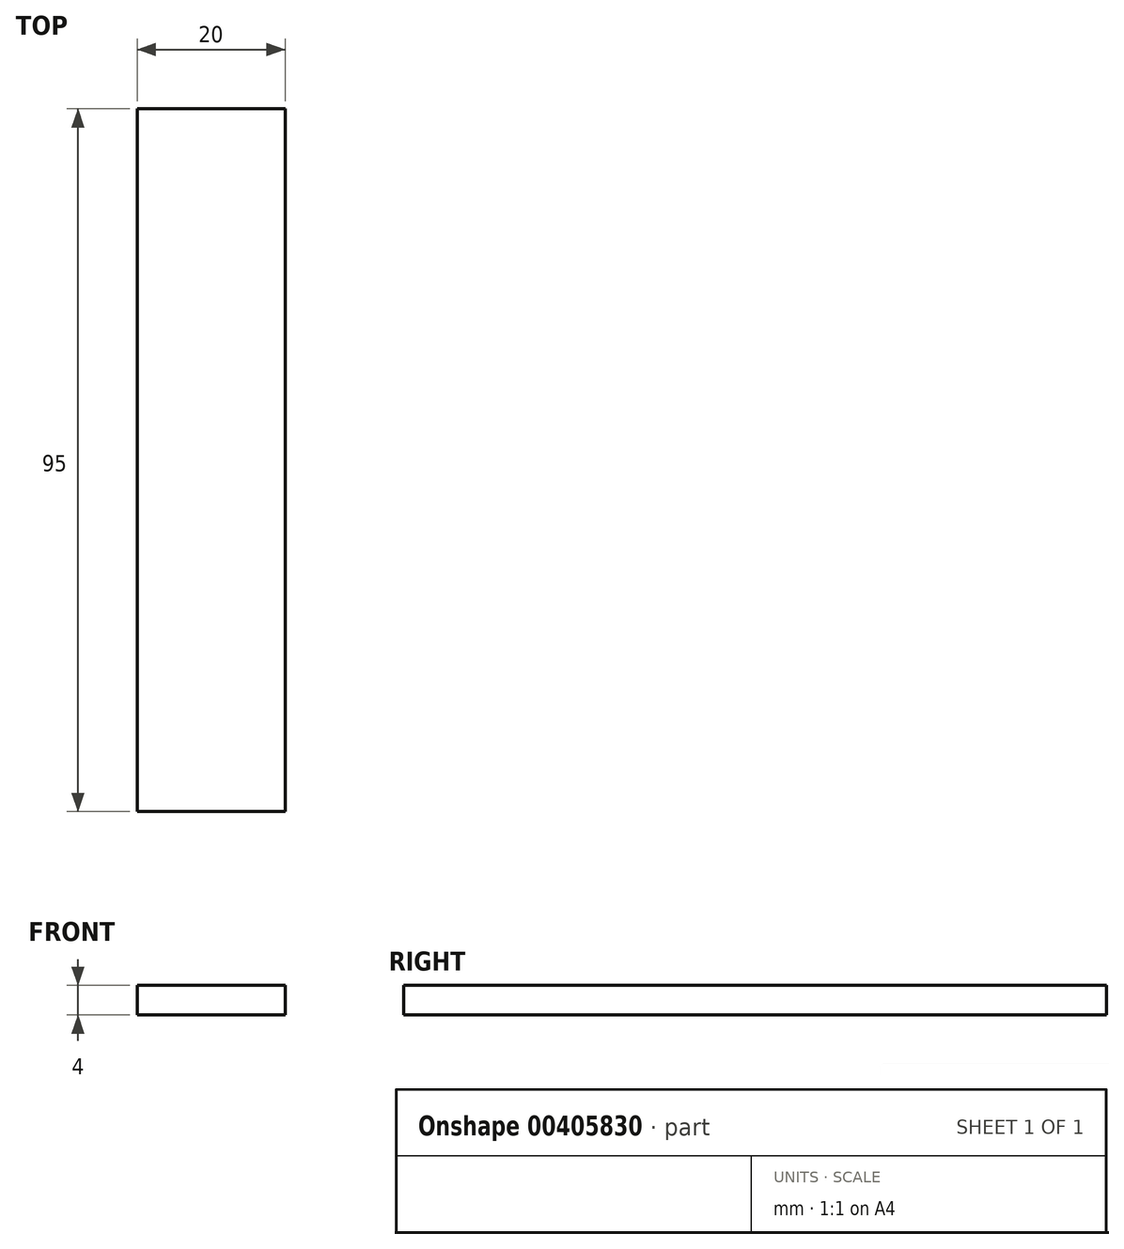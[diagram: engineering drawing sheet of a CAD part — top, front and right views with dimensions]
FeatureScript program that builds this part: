
annotation { "Feature Type Name" : "Feature", "Feature Type Description" : "" }
export const myFeature = defineFeature(function(context is Context, id is Id, definition is map)
    precondition{}
    {
        {
            var Q0;
            Q0=qCreatedBy(makeId("Top.planeOp"),FACE);
            var sketch = newSketch(context, id + "F0", { "sketchPlane" : qUnion([Q0])});
            skLineSegment(sketch, "E0.bottom", {"start": v(-10, 47.5) * mm, "end": v(10, 47.5) * mm});
            skLineSegment(sketch, "E0.top", {"start": v(-10, -47.5) * mm, "end": v(10, -47.5) * mm});
            skLineSegment(sketch, "E0.left", {"start": v(-10, 47.5) * mm, "end": v(-10, -47.5) * mm});
            skLineSegment(sketch, "E0.right", {"start": v(10, 47.5) * mm, "end": v(10, -47.5) * mm});
            skPoint(sketch, "E0.middle", {"position": v(0, 0) * mm});
            skSolve(sketch);
        }
        {
            var Q0;
            Q0=makeQuery(id+"F0.imprint","IMPRINT",FACE,{"disambiguationData":[TD([[makeQuery(id+"F0.imprint","IMPRINT",EDGE,{"derivedFrom":sQuery(id+"F0.wireOp",EDGE,"E0.bottom")}),-1.0]])]});
            extrude(context, id + "F1", {"entities" : qUnion([Q0]), "depth" : 4 * mm});
        }
    });
